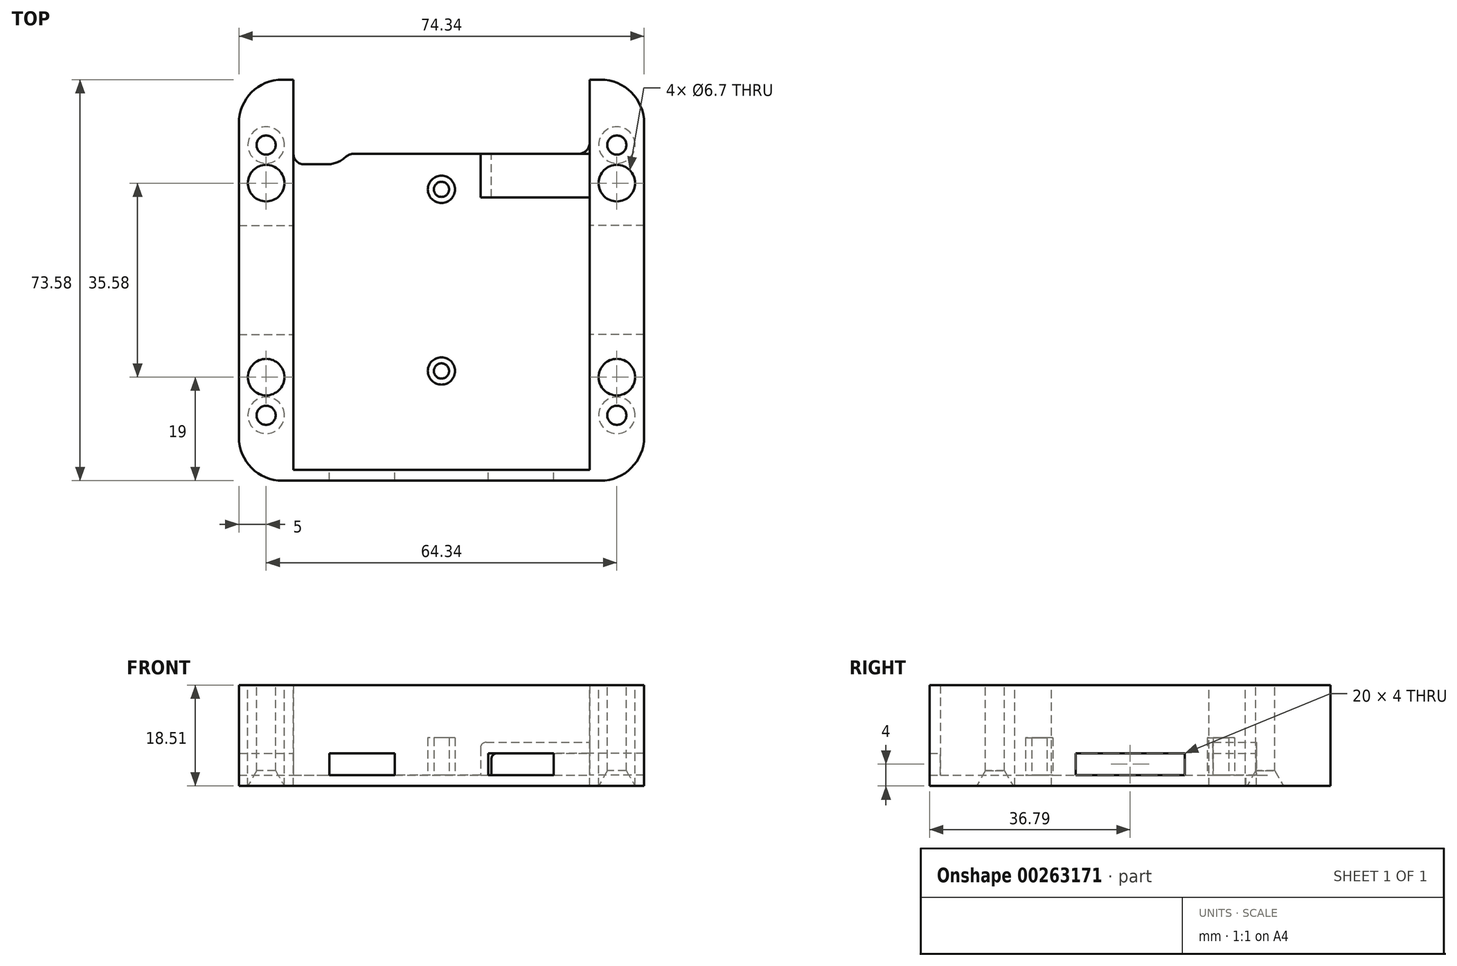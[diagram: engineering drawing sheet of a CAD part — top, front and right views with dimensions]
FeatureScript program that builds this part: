
annotation { "Feature Type Name" : "Feature", "Feature Type Description" : "" }
export const myFeature = defineFeature(function(context is Context, id is Id, definition is map)
    precondition{}
    {
        {
            var Q0;
            Q0=qCreatedBy(makeId("Top.planeOp"),FACE);
            var sketch = newSketch(context, id + "F0", { "sketchPlane" : qUnion([Q0])});
            skLineSegment(sketch, "E0.bottom", {"start": v(8, 0) * mm, "end": v(66.34, 0) * mm, "construction": true});
            skLineSegment(sketch, "E0.top", {"start": v(8, 73.58) * mm, "end": v(66.34, 73.58) * mm, "construction": true});
            skLineSegment(sketch, "E0.left", {"start": v(0, 8) * mm, "end": v(0, 65.58) * mm, "construction": true});
            skLineSegment(sketch, "E0.right", {"start": v(74.34, 8) * mm, "end": v(74.34, 65.58) * mm, "construction": true});
            skArc(sketch, "E1", {"start": v(8, 73.58) * mm, "mid": v(2.34, 71.24) * mm, "end": v(0, 65.58) * mm, "construction": true});
            skArc(sketch, "E2", {"start": v(0, 8) * mm, "mid": v(2.34, 2.34) * mm, "end": v(8, 0) * mm, "construction": true});
            skArc(sketch, "E3", {"start": v(74.34, 65.58) * mm, "mid": v(72, 71.24) * mm, "end": v(66.34, 73.58) * mm, "construction": true});
            skArc(sketch, "E4", {"start": v(66.34, 0) * mm, "mid": v(72, 2.34) * mm, "end": v(74.34, 8) * mm, "construction": true});
            skCircle(sketch, "E5", {"center": v(5, 61.58) * mm, "radius": 1.4 * mm, "construction": true});
            skCircle(sketch, "E6", {"center": v(5, 54.58) * mm, "radius": 3.35 * mm, "construction": true});
            skLineSegment(sketch, "E7", {"start": v(0, 36.8) * mm, "end": v(74.34, 36.8) * mm, "construction": true});
            skLineSegment(sketch, "E8", {"start": v(37.17, 73.58) * mm, "end": v(37.17, 0) * mm, "construction": true});
            skCircle(sketch, "E9.MirrorC", {"center": v(69.34, 54.58) * mm, "radius": 3.35 * mm, "construction": true});
            skCircle(sketch, "E10.MirrorC", {"center": v(69.34, 61.58) * mm, "radius": 1.4 * mm, "construction": true});
            skCircle(sketch, "E11.MirrorC", {"center": v(69.34, 12) * mm, "radius": 1.4 * mm, "construction": true});
            skCircle(sketch, "E12.MirrorC", {"center": v(69.34, 19) * mm, "radius": 3.35 * mm, "construction": true});
            skCircle(sketch, "E13.MirrorC", {"center": v(5, 19) * mm, "radius": 3.35 * mm, "construction": true});
            skCircle(sketch, "E14.MirrorC", {"center": v(5, 12) * mm, "radius": 1.4 * mm, "construction": true});
            skCircle(sketch, "E15", {"center": v(16.14, 63.03) * mm, "radius": 3.3 * mm, "construction": true});
            skLineSegment(sketch, "E16.bottom", {"start": v(10.83, 54.55) * mm, "end": v(15.24, 54.55) * mm, "construction": true});
            skLineSegment(sketch, "E16.top", {"start": v(10.84, 5.31) * mm, "end": v(15.25, 5.31) * mm, "construction": true});
            skLineSegment(sketch, "E16.left", {"start": v(10.83, 54.55) * mm, "end": v(10.83, 5.31) * mm, "construction": true});
            skLineSegment(sketch, "E16.right", {"start": v(15.24, 54.55) * mm, "end": v(15.24, 5.31) * mm, "construction": true});
            skLineSegment(sketch, "E17.bottom", {"start": v(32.84, 69.48) * mm, "end": v(62.84, 69.48) * mm, "construction": true});
            skLineSegment(sketch, "E17.top", {"start": v(32.84, 59.98) * mm, "end": v(62.84, 59.98) * mm, "construction": true});
            skLineSegment(sketch, "E17.left", {"start": v(32.84, 69.48) * mm, "end": v(32.84, 59.98) * mm, "construction": true});
            skLineSegment(sketch, "E17.right", {"start": v(62.84, 69.48) * mm, "end": v(62.84, 59.98) * mm, "construction": true});
            skLineSegment(sketch, "E18.bottom", {"start": v(59.1, 45.4) * mm, "end": v(63.5, 45.4) * mm, "construction": true});
            skLineSegment(sketch, "E18.top", {"start": v(59.1, 5.3) * mm, "end": v(63.5, 5.3) * mm, "construction": true});
            skLineSegment(sketch, "E18.left", {"start": v(59.1, 45.4) * mm, "end": v(59.1, 5.3) * mm, "construction": true});
            skLineSegment(sketch, "E18.right", {"start": v(63.5, 45.4) * mm, "end": v(63.5, 5.3) * mm, "construction": true});
            skLineSegment(sketch, "E19.bottom", {"start": v(19.88, 57) * mm, "end": v(31.88, 57) * mm, "construction": true});
            skLineSegment(sketch, "E19.top", {"start": v(19.88, 41) * mm, "end": v(21.13, 41) * mm, "construction": true});
            skLineSegment(sketch, "E19.left", {"start": v(19.88, 57) * mm, "end": v(19.88, 41) * mm, "construction": true});
            skLineSegment(sketch, "E19.right", {"start": v(31.88, 57) * mm, "end": v(31.88, 41) * mm, "construction": true});
            skLineSegment(sketch, "E20", {"start": v(21.13, 41) * mm, "end": v(21.14, 8.5) * mm, "construction": true});
            skLineSegment(sketch, "E21", {"start": v(21.14, 8.5) * mm, "end": v(30.64, 8.5) * mm, "construction": true});
            skLineSegment(sketch, "E22", {"start": v(30.64, 8.5) * mm, "end": v(30.64, 41) * mm, "construction": true});
            skLineSegment(sketch, "E23.trimOffspring", {"start": v(30.64, 41) * mm, "end": v(31.88, 41) * mm, "construction": true});
            skSolve(sketch);
        }
        {
            var Q0;
            Q0=qCreatedBy(makeId("Top.planeOp"),FACE);
            var sketch = newSketch(context, id + "F1", { "sketchPlane" : qUnion([Q0])});
            skLineSegment(sketch, "E24", {"start": v(0, 65.58) * mm, "end": v(0, 8) * mm});
            skLineSegment(sketch, "E25", {"start": v(74.34, 65.58) * mm, "end": v(74.34, 8) * mm});
            skCircle(sketch, "E26", {"center": v(5, 61.58) * mm, "radius": 1.75 * mm});
            skCircle(sketch, "E27", {"center": v(5, 12) * mm, "radius": 1.75 * mm});
            skCircle(sketch, "E28", {"center": v(69.34, 12) * mm, "radius": 1.75 * mm});
            skCircle(sketch, "E29", {"center": v(69.34, 61.58) * mm, "radius": 1.75 * mm});
            skCircle(sketch, "E30", {"center": v(5, 54.58) * mm, "radius": 3.35 * mm});
            skCircle(sketch, "E31", {"center": v(5, 19) * mm, "radius": 3.35 * mm});
            skCircle(sketch, "E32", {"center": v(69.34, 19) * mm, "radius": 3.35 * mm});
            skCircle(sketch, "E33", {"center": v(69.34, 54.58) * mm, "radius": 3.35 * mm});
            skLineSegment(sketch, "E34", {"start": v(8, 73.58) * mm, "end": v(10, 73.58) * mm});
            skArc(sketch, "E35", {"start": v(8, 73.58) * mm, "mid": v(2.34, 71.24) * mm, "end": v(0, 65.58) * mm});
            skArc(sketch, "E36", {"start": v(74.34, 65.58) * mm, "mid": v(72, 71.24) * mm, "end": v(66.34, 73.58) * mm});
            skLineSegment(sketch, "E37", {"start": v(8, 0) * mm, "end": v(66.34, 0) * mm});
            skArc(sketch, "E38", {"start": v(0, 8) * mm, "mid": v(2.34, 2.34) * mm, "end": v(8, 0) * mm});
            skArc(sketch, "E39", {"start": v(66.34, 0) * mm, "mid": v(72, 2.34) * mm, "end": v(74.34, 8) * mm});
            skArc(sketch, "E40", {"start": v(16.14, 58.03) * mm, "mid": v(17.94, 58.37) * mm, "end": v(19.5, 59.33) * mm});
            skLineSegment(sketch, "E41", {"start": v(64.34, 59.98) * mm, "end": v(21.18, 59.98) * mm});
            skArc(sketch, "E42", {"start": v(21.18, 59.98) * mm, "mid": v(20.28, 59.81) * mm, "end": v(19.5, 59.33) * mm});
            skLineSegment(sketch, "E43", {"start": v(64.34, 59.98) * mm, "end": v(64.34, 73.58) * mm});
            skLineSegment(sketch, "E44", {"start": v(66.34, 73.58) * mm, "end": v(64.34, 73.58) * mm});
            skLineSegment(sketch, "E45", {"start": v(10, 73.58) * mm, "end": v(10, 58.03) * mm});
            skLineSegment(sketch, "E46", {"start": v(10, 58.03) * mm, "end": v(16.14, 58.03) * mm});
            skSolve(sketch);
        }
        {
            var Q0;
            Q0 = qSketchRegion(id + "F1", true);
            extrude(context, id + "F2", {"entities" : qUnion([Q0]), "oppositeDirection" : true, "depth" : 2 * mm});
        }
        {
            var Q0;
            Q0=makeQuery(id+"F2.opExtrude","SWEPT_EDGE",EDGE,{"disambiguationData":[OSD([sQuery(id+"F1.wireOp",EDGE,"E45"),sQuery(id+"F1.wireOp",EDGE,"E46")])]});
            var Q1;
            Q1=makeQuery(id+"F2.opExtrude","SWEPT_EDGE",EDGE,{"disambiguationData":[OSD([sQuery(id+"F1.wireOp",EDGE,"E41"),sQuery(id+"F1.wireOp",EDGE,"E43")])]});
            fillet(context, id + "F3", {"entities" : qUnion([Q0, Q1]), "radius" : 2 * mm, "tangentPropagation" : true, "allowEdgeOverflow" : false});
        }
        {
            var Q0;
            Q0=makeQuery(id+"F2.opExtrude","CAP_FACE",FACE,{"disambiguationData":[OSD([sQuery(id+"F1.wireOp",EDGE,"E24"),sQuery(id+"F1.wireOp",EDGE,"E25"),sQuery(id+"F1.wireOp",EDGE,"E26"),sQuery(id+"F1.wireOp",EDGE,"E27"),sQuery(id+"F1.wireOp",EDGE,"E28"),sQuery(id+"F1.wireOp",EDGE,"E29"),sQuery(id+"F1.wireOp",EDGE,"E30"),sQuery(id+"F1.wireOp",EDGE,"E31"),sQuery(id+"F1.wireOp",EDGE,"E32"),sQuery(id+"F1.wireOp",EDGE,"E33"),sQuery(id+"F1.wireOp",EDGE,"E34"),sQuery(id+"F1.wireOp",EDGE,"E35"),sQuery(id+"F1.wireOp",EDGE,"E36"),sQuery(id+"F1.wireOp",EDGE,"E37"),sQuery(id+"F1.wireOp",EDGE,"E38"),sQuery(id+"F1.wireOp",EDGE,"E39"),sQuery(id+"F1.wireOp",EDGE,"E40"),sQuery(id+"F1.wireOp",EDGE,"szp27tM4-Ggn2-58AR-YqNy-7nc7cWW06Emm"),sQuery(id+"F1.wireOp",EDGE,"0f7bfab5-27f3-44fa-b1d4-cae2101ceb6e.trimOffspring"),sQuery(id+"F1.wireOp",EDGE,"bU7Ev4i4-ZTTS-p5M7-DCLq-JKvuHiUkPX25"),sQuery(id+"F1.wireOp",EDGE,"E41"),sQuery(id+"F1.wireOp",EDGE,"E42")])],"isStart":true});
            var sketch = newSketch(context, id + "F4", { "sketchPlane" : qUnion([Q0])});
            skLineSegment(sketch, "E47", {"start": v(0, 65.58) * mm, "end": v(0, 8) * mm});
            skArc(sketch, "E48", {"start": v(0, 8) * mm, "mid": v(2.34, 2.34) * mm, "end": v(8, 0) * mm});
            skLineSegment(sketch, "E49", {"start": v(8, 0) * mm, "end": v(66.34, 0) * mm});
            skArc(sketch, "E50", {"start": v(66.34, 0) * mm, "mid": v(72, 2.34) * mm, "end": v(74.34, 8) * mm});
            skLineSegment(sketch, "E51", {"start": v(64.34, 73.58) * mm, "end": v(64.34, 2) * mm});
            skLineSegment(sketch, "E52", {"start": v(10, 2) * mm, "end": v(64.34, 2) * mm});
            skLineSegment(sketch, "E53", {"start": v(10, 2) * mm, "end": v(10, 73.58) * mm});
            skArc(sketch, "E54", {"start": v(8, 73.58) * mm, "mid": v(2.34, 71.24) * mm, "end": v(0, 65.58) * mm});
            skLineSegment(sketch, "E55", {"start": v(8, 73.58) * mm, "end": v(10, 73.58) * mm});
            skArc(sketch, "E56", {"start": v(74.34, 65.58) * mm, "mid": v(72, 71.24) * mm, "end": v(66.34, 73.58) * mm});
            skLineSegment(sketch, "E57", {"start": v(64.34, 73.58) * mm, "end": v(66.34, 73.58) * mm});
            skLineSegment(sketch, "E58", {"start": v(74.34, 65.58) * mm, "end": v(74.34, 8) * mm});
            skCircle(sketch, "E59", {"center": v(5, 61.58) * mm, "radius": 1.75 * mm});
            skCircle(sketch, "E60", {"center": v(5, 54.58) * mm, "radius": 3.35 * mm});
            skCircle(sketch, "E61", {"center": v(5, 19) * mm, "radius": 3.35 * mm});
            skCircle(sketch, "E62", {"center": v(5, 12) * mm, "radius": 1.75 * mm});
            skCircle(sketch, "E63", {"center": v(69.34, 12) * mm, "radius": 1.75 * mm});
            skCircle(sketch, "E64", {"center": v(69.34, 19) * mm, "radius": 3.35 * mm});
            skCircle(sketch, "E65", {"center": v(69.34, 61.58) * mm, "radius": 1.75 * mm});
            skCircle(sketch, "E66", {"center": v(69.34, 54.58) * mm, "radius": 3.35 * mm});
            skSolve(sketch);
        }
        {
            var Q0;
            Q0 = qSketchRegion(id + "F4", true);
            extrude(context, id + "F5", {"entities" : qUnion([Q0]), "operationType" : NewBodyOperationType.ADD, "depth" : 16.51 * mm});
        }
        {
            var Q0;
            Q0=makeQuery(id+"F2.opExtrude","CAP_EDGE",EDGE,{"disambiguationData":[OSD([sQuery(id+"F1.wireOp",EDGE,"E26")])],"isStart":false});
            var Q1;
            Q1=makeQuery(id+"F2.opExtrude","CAP_EDGE",EDGE,{"disambiguationData":[OSD([sQuery(id+"F1.wireOp",EDGE,"E27")])],"isStart":false});
            var Q2;
            Q2=makeQuery(id+"F2.opExtrude","CAP_EDGE",EDGE,{"disambiguationData":[OSD([sQuery(id+"F1.wireOp",EDGE,"E28")])],"isStart":false});
            var Q3;
            Q3=makeQuery(id+"F2.opExtrude","CAP_EDGE",EDGE,{"disambiguationData":[OSD([sQuery(id+"F1.wireOp",EDGE,"E29")])],"isStart":false});
            chamfer(context, id + "F6", {"entities" : qUnion([Q0, Q1, Q2, Q3]), "chamferType" : ChamferType.TWO_OFFSETS, "width1" : 1.6 * mm, "oppositeDirection" : false, "width2" : 2.8 * mm, "tangentPropagation" : true});
        }
        {
            var Q0;
            Q0=makeQuery(id+"F2.opExtrude","CAP_FACE",FACE,{"disambiguationData":[OSD([sQuery(id+"F1.wireOp",EDGE,"E24"),sQuery(id+"F1.wireOp",EDGE,"E25"),sQuery(id+"F1.wireOp",EDGE,"E26"),sQuery(id+"F1.wireOp",EDGE,"E27"),sQuery(id+"F1.wireOp",EDGE,"E28"),sQuery(id+"F1.wireOp",EDGE,"E29"),sQuery(id+"F1.wireOp",EDGE,"E30"),sQuery(id+"F1.wireOp",EDGE,"E31"),sQuery(id+"F1.wireOp",EDGE,"E32"),sQuery(id+"F1.wireOp",EDGE,"E33"),sQuery(id+"F1.wireOp",EDGE,"E34"),sQuery(id+"F1.wireOp",EDGE,"E35"),sQuery(id+"F1.wireOp",EDGE,"E36"),sQuery(id+"F1.wireOp",EDGE,"E37"),sQuery(id+"F1.wireOp",EDGE,"E38"),sQuery(id+"F1.wireOp",EDGE,"E39"),sQuery(id+"F1.wireOp",EDGE,"E40"),sQuery(id+"F1.wireOp",EDGE,"E41"),sQuery(id+"F1.wireOp",EDGE,"E42"),sQuery(id+"F1.wireOp",EDGE,"E43"),sQuery(id+"F1.wireOp",EDGE,"E44"),sQuery(id+"F1.wireOp",EDGE,"E45"),sQuery(id+"F1.wireOp",EDGE,"E46")])],"isStart":true});
            var sketch = newSketch(context, id + "F7", { "sketchPlane" : qUnion([Q0])});
            skLineSegment(sketch, "E67.bottom", {"start": v(31.67, 49.45) * mm, "end": v(42.67, 49.45) * mm, "construction": true});
            skLineSegment(sketch, "E67.top", {"start": v(31.67, 24.13) * mm, "end": v(42.67, 24.13) * mm, "construction": true});
            skLineSegment(sketch, "E67.left", {"start": v(31.67, 49.45) * mm, "end": v(31.67, 24.13) * mm, "construction": true});
            skLineSegment(sketch, "E67.right", {"start": v(42.67, 49.45) * mm, "end": v(42.67, 24.13) * mm, "construction": true});
            skCircle(sketch, "E68", {"center": v(37.17, 53.45) * mm, "radius": 2.5 * mm});
            skCircle(sketch, "E69", {"center": v(37.17, 20.13) * mm, "radius": 2.5 * mm});
            skCircle(sketch, "E70", {"center": v(37.17, 53.45) * mm, "radius": 1.4 * mm});
            skCircle(sketch, "E71", {"center": v(37.17, 20.13) * mm, "radius": 1.4 * mm});
            skSolve(sketch);
        }
        {
            var Q0;
            Q0 = qSketchRegion(id + "F7", true);
            extrude(context, id + "F8", {"entities" : qUnion([Q0]), "operationType" : NewBodyOperationType.ADD, "depth" : 6.85 * mm});
        }
        {
            var Q0;
            Q0=makeQuery(id+"F5.boolean.opBoolean","MERGE",FACE,{"derivedFrom":[makeQuery(id+"F2.opExtrude","SWEPT_FACE",FACE,{"disambiguationData":[OSD([sQuery(id+"F1.wireOp",EDGE,"E45")])]}),makeQuery(id+"F5.opExtrude","SWEPT_FACE",FACE,{"disambiguationData":[OSD([sQuery(id+"F4.wireOp",EDGE,"E53")])]})]});
            var sketch = newSketch(context, id + "F9", { "sketchPlane" : qUnion([Q0])});
            skLineSegment(sketch, "E72.bottom", {"start": v(26.8, 4) * mm, "end": v(46.8, 4) * mm});
            skLineSegment(sketch, "E72.top", {"start": v(26.8, 0) * mm, "end": v(46.8, 0) * mm});
            skLineSegment(sketch, "E72.left", {"start": v(26.8, 4) * mm, "end": v(26.8, 0) * mm});
            skLineSegment(sketch, "E72.right", {"start": v(46.8, 4) * mm, "end": v(46.8, 0) * mm});
            skLineSegment(sketch, "E73", {"start": v(36.8, 4) * mm, "end": v(36.8, 0) * mm, "construction": true});
            skSolve(sketch);
        }
        {
            var Q0;
            Q0 = qSketchRegion(id + "F9", true);
            extrude(context, id + "F10", {"entities" : qUnion([Q0]), "operationType" : NewBodyOperationType.REMOVE, "endBound" : BoundingType.THROUGH_ALL, "oppositeDirection" : true, "depth" : 25 * mm});
        }
        {
            var Q0;
            Q0=makeQuery(id+"F5.boolean.opBoolean","MERGE",FACE,{"derivedFrom":[makeQuery(id+"F2.opExtrude","SWEPT_FACE",FACE,{"disambiguationData":[OSD([sQuery(id+"F1.wireOp",EDGE,"E43")])]}),makeQuery(id+"F5.opExtrude","SWEPT_FACE",FACE,{"disambiguationData":[OSD([sQuery(id+"F4.wireOp",EDGE,"E51")])]})]});
            var sketch = newSketch(context, id + "F11", { "sketchPlane" : qUnion([Q0])});
            skLineSegment(sketch, "E74.bottom", {"start": v(-46.79, 0) * mm, "end": v(-26.79, 0) * mm});
            skLineSegment(sketch, "E74.top", {"start": v(-46.79, 4) * mm, "end": v(-26.79, 4) * mm});
            skLineSegment(sketch, "E74.left", {"start": v(-46.79, 0) * mm, "end": v(-46.79, 4) * mm});
            skLineSegment(sketch, "E74.right", {"start": v(-26.79, 0) * mm, "end": v(-26.79, 4) * mm});
            skLineSegment(sketch, "E75", {"start": v(-36.79, 4) * mm, "end": v(-36.79, 0) * mm, "construction": true});
            skSolve(sketch);
        }
        {
            var Q0;
            Q0 = qSketchRegion(id + "F11", true);
            extrude(context, id + "F12", {"entities" : qUnion([Q0]), "operationType" : NewBodyOperationType.REMOVE, "endBound" : BoundingType.THROUGH_ALL, "oppositeDirection" : true, "depth" : 25 * mm});
        }
        {
            var Q0;
            Q0=makeQuery(id+"F5.opExtrude","SWEPT_FACE",FACE,{"disambiguationData":[OSD([sQuery(id+"F4.wireOp",EDGE,"E52")])]});
            var sketch = newSketch(context, id + "F13", { "sketchPlane" : qUnion([Q0])});
            skLineSegment(sketch, "E76", {"start": v(-37.17, 16.51) * mm, "end": v(-37.17, 0) * mm, "construction": true});
            skLineSegment(sketch, "E77.bottom", {"start": v(-57.76, 0) * mm, "end": v(-45.76, 0) * mm});
            skLineSegment(sketch, "E77.top", {"start": v(-57.76, 4) * mm, "end": v(-45.76, 4) * mm});
            skLineSegment(sketch, "E77.left", {"start": v(-57.76, 0) * mm, "end": v(-57.76, 4) * mm});
            skLineSegment(sketch, "E77.right", {"start": v(-45.76, 0) * mm, "end": v(-45.76, 4) * mm});
            skLineSegment(sketch, "E78.MirrorCS", {"start": v(-28.59, 0) * mm, "end": v(-28.59, 4) * mm});
            skLineSegment(sketch, "E79.MirrorCS", {"start": v(-16.58, 0) * mm, "end": v(-16.58, 4) * mm});
            skLineSegment(sketch, "E80.MirrorCS", {"start": v(-16.59, 4) * mm, "end": v(-28.59, 4) * mm});
            skLineSegment(sketch, "E81.MirrorCS", {"start": v(-16.58, 0) * mm, "end": v(-28.59, 0) * mm});
            skSolve(sketch);
        }
        {
            var Q0;
            Q0 = qSketchRegion(id + "F13", true);
            extrude(context, id + "F14", {"entities" : qUnion([Q0]), "operationType" : NewBodyOperationType.REMOVE, "endBound" : BoundingType.THROUGH_ALL, "oppositeDirection" : true, "depth" : 25 * mm});
        }
        {
            var Q0;
            {var subQ0=sQuery(id+"F1.wireOp",EDGE,"E41");var subQ1=sQuery(id+"F1.wireOp",EDGE,"E46");var subQ2=sQuery(id+"F1.wireOp",EDGE,"E45");var subQ3=sQuery(id+"F1.wireOp",EDGE,"E43");var subQ4=sQuery(id+"F1.wireOp",EDGE,"E42");var subQ5=sQuery(id+"F1.wireOp",EDGE,"E40");Q0=makeQuery(id+"F14.boolean.opBoolean","MERGE",FACE,{"derivedFrom":[makeQuery(id+"F12.boolean.opBoolean","MERGE",FACE,{"derivedFrom":[makeQuery(id+"F10.boolean.opBoolean","MERGE",FACE,{"derivedFrom":[makeQuery(id+"F8.boolean.opBoolean","SPLIT",FACE,{"disambiguationData":[TD([makeQuery(id+"F2.opExtrude","SWEPT_FACE",FACE,{"disambiguationData":[OSD([subQ5])]})])],"derivedFrom":makeQuery(id+"F2.opExtrude","CAP_FACE",FACE,{"disambiguationData":[OSD([sQuery(id+"F1.wireOp",EDGE,"E24"),sQuery(id+"F1.wireOp",EDGE,"E25"),sQuery(id+"F1.wireOp",EDGE,"E26"),sQuery(id+"F1.wireOp",EDGE,"E27"),sQuery(id+"F1.wireOp",EDGE,"E28"),sQuery(id+"F1.wireOp",EDGE,"E29"),sQuery(id+"F1.wireOp",EDGE,"E30"),sQuery(id+"F1.wireOp",EDGE,"E31"),sQuery(id+"F1.wireOp",EDGE,"E32"),sQuery(id+"F1.wireOp",EDGE,"E33"),sQuery(id+"F1.wireOp",EDGE,"E34"),sQuery(id+"F1.wireOp",EDGE,"E35"),sQuery(id+"F1.wireOp",EDGE,"E36"),sQuery(id+"F1.wireOp",EDGE,"E37"),sQuery(id+"F1.wireOp",EDGE,"E38"),sQuery(id+"F1.wireOp",EDGE,"E39"),subQ5,subQ0,subQ4,subQ3,sQuery(id+"F1.wireOp",EDGE,"E44"),subQ2,subQ1])],"isStart":true})}),makeQuery(id+"F10.opExtrude","SWEPT_FACE",FACE,{"disambiguationData":[OSD([sQuery(id+"F9.wireOp",EDGE,"E72.top")])]})]}),makeQuery(id+"F12.opExtrude","SWEPT_FACE",FACE,{"disambiguationData":[OSD([sQuery(id+"F11.wireOp",EDGE,"E74.bottom")])]})]}),makeQuery(id+"F14.opExtrude","SWEPT_FACE",FACE,{"disambiguationData":[OSD([sQuery(id+"F13.wireOp",EDGE,"E77.bottom")])]}),makeQuery(id+"F14.opExtrude","SWEPT_FACE",FACE,{"disambiguationData":[OSD([sQuery(id+"F13.wireOp",EDGE,"E81.MirrorCS")])]})]});}
            var sketch = newSketch(context, id + "F15", { "sketchPlane" : qUnion([Q0])});
            skLineSegment(sketch, "E82.bottom", {"start": v(44.34, 59.98) * mm, "end": v(64.34, 59.98) * mm});
            skLineSegment(sketch, "E82.top", {"start": v(44.34, 51.98) * mm, "end": v(64.34, 51.98) * mm});
            skLineSegment(sketch, "E82.left", {"start": v(44.34, 59.98) * mm, "end": v(44.34, 51.98) * mm});
            skLineSegment(sketch, "E82.right", {"start": v(64.34, 59.98) * mm, "end": v(64.34, 51.98) * mm});
            skSolve(sketch);
        }
        {
            var Q0;
            Q0 = qSketchRegion(id + "F15", true);
            extrude(context, id + "F16", {"entities" : qUnion([Q0]), "operationType" : NewBodyOperationType.ADD, "depth" : 6 * mm});
        }
        {
            var Q0;
            Q0=makeQuery(id+"F16.boolean.opBoolean","MERGE",FACE,{"derivedFrom":[makeQuery(id+"F2.opExtrude","SWEPT_FACE",FACE,{"disambiguationData":[OSD([sQuery(id+"F1.wireOp",EDGE,"E41")])]}),makeQuery(id+"F16.opExtrude","SWEPT_FACE",FACE,{"disambiguationData":[OSD([sQuery(id+"F15.wireOp",EDGE,"E82.bottom")])]})]});
            var sketch = newSketch(context, id + "F17", { "sketchPlane" : qUnion([Q0])});
            skLineSegment(sketch, "E83.bottom", {"start": v(-64.34, 0) * mm, "end": v(-46.34, 0) * mm});
            skLineSegment(sketch, "E83.top", {"start": v(-64.34, 4) * mm, "end": v(-46.34, 4) * mm});
            skLineSegment(sketch, "E83.left", {"start": v(-64.34, 0) * mm, "end": v(-64.34, 4) * mm});
            skLineSegment(sketch, "E83.right", {"start": v(-46.34, 0) * mm, "end": v(-46.34, 4) * mm});
            skSolve(sketch);
        }
        {
            var Q0;
            Q0 = qSketchRegion(id + "F17", true);
            var Q1;
            Q1=makeQuery(id+"F16.opExtrude","SWEPT_FACE",FACE,{"disambiguationData":[OSD([sQuery(id+"F15.wireOp",EDGE,"E82.top")])]});
            extrude(context, id + "F18", {"entities" : qUnion([Q0]), "operationType" : NewBodyOperationType.REMOVE, "endBound" : BoundingType.UP_TO_SURFACE, "oppositeDirection" : true, "endBoundEntityFace" : qUnion([Q1]), "depth" : 25 * mm});
        }
        {
            var Q0;
            Q0=makeQuery(id+"F18.boolean.opBoolean","COPY",EDGE,{"derivedFrom":makeQuery(id+"F18.opExtrude","SWEPT_EDGE",EDGE,{"disambiguationData":[OSD([sQuery(id+"F17.wireOp",EDGE,"E83.top"),sQuery(id+"F17.wireOp",EDGE,"E83.right")])]})});
            var Q1;
            Q1=makeQuery(id+"F16.opExtrude","CAP_EDGE",EDGE,{"disambiguationData":[OSD([sQuery(id+"F15.wireOp",EDGE,"E82.left")])],"isStart":false});
            fillet(context, id + "F19", {"entities" : qUnion([Q0, Q1]), "radius" : 1 * mm, "tangentPropagation" : true, "allowEdgeOverflow" : false});
        }
    });
